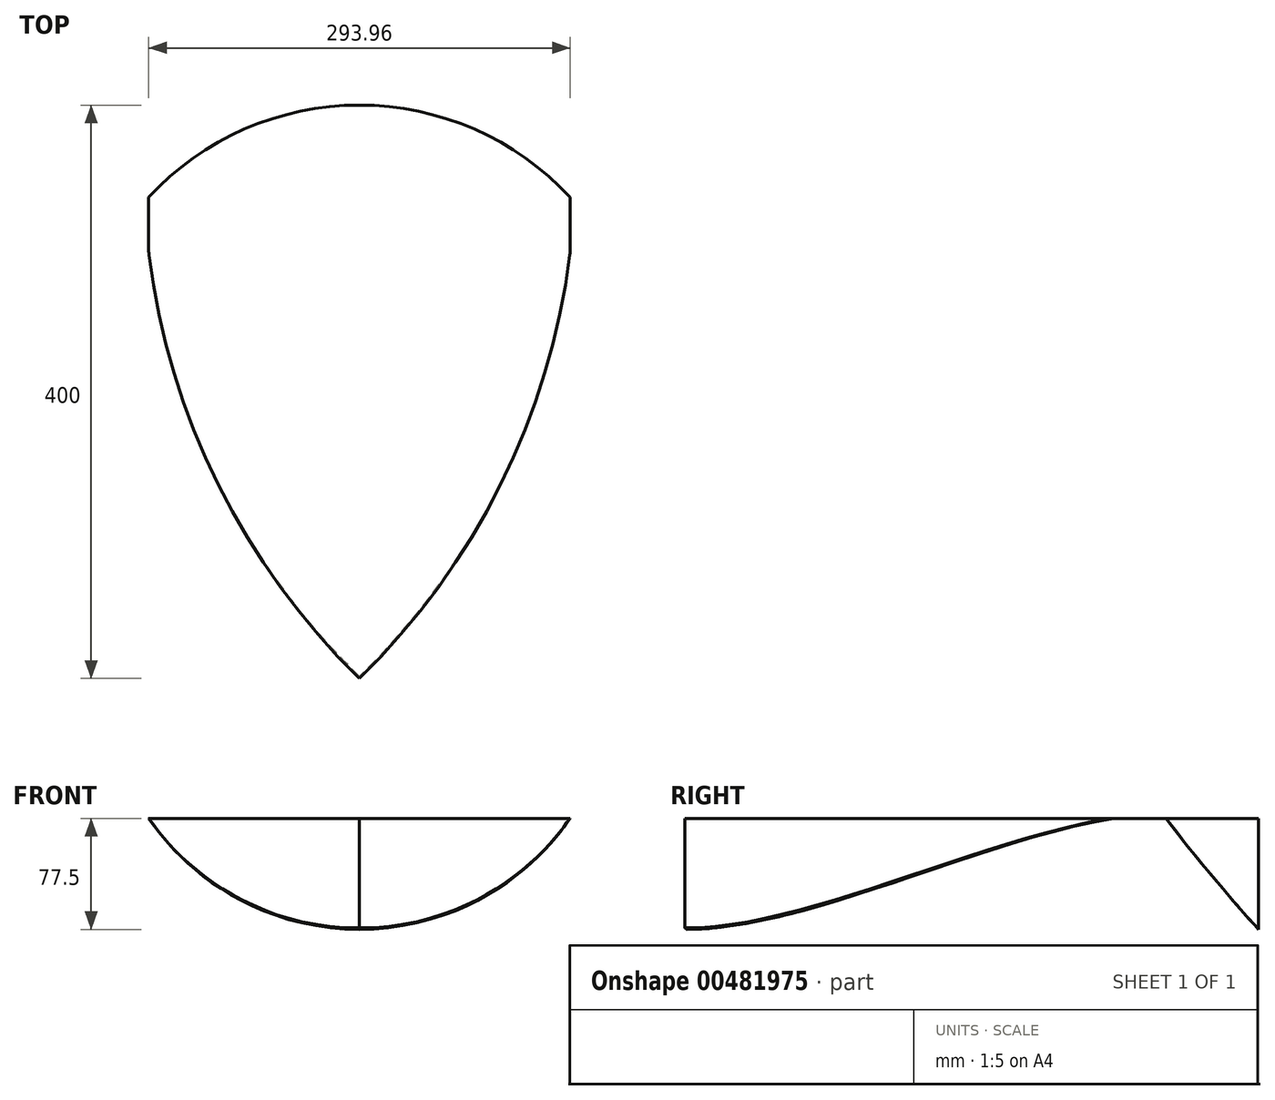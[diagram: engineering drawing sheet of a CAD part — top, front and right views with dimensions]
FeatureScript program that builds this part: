
annotation { "Feature Type Name" : "Feature", "Feature Type Description" : "" }
export const myFeature = defineFeature(function(context is Context, id is Id, definition is map)
    precondition{}
    {
        {
            var Q0;
            Q0=qCreatedBy(makeId("Front.planeOp"),FACE);
            var sketch = newSketch(context, id + "F0", { "sketchPlane" : qUnion([Q0])});
            skLineSegment(sketch, "E0", {"start": v(-150, 80) * mm, "end": v(150, 80) * mm});
            skLineSegment(sketch, "E1", {"start": v(0, 80) * mm, "end": v(0, 0) * mm, "construction": true});
            skArc(sketch, "E2", {"start": v(-150, 80) * mm, "mid": v(0, 0) * mm, "end": v(150, 80) * mm});
            skLineSegment(sketch, "E3", {"start": v(0, 0) * mm, "end": v(-231.09, 0) * mm, "construction": true});
            skLineSegment(sketch, "E4", {"start": v(-154.42, 61.21) * mm, "end": v(-48.4, 0) * mm, "construction": true});
            skSolve(sketch);
        }
        {
            var Q0;
            Q0=makeQuery(id+"F0.imprint","IMPRINT",FACE,{"disambiguationData":[TD([[makeQuery(id+"F0.imprint","IMPRINT",EDGE,{"derivedFrom":sQuery(id+"F0.wireOp",EDGE,"E0")}),-1.0]])]});
            extrude(context, id + "F1", {"entities" : qUnion([Q0]), "depth" : 400 * mm});
        }
        {
            var Q0;
            Q0=makeQuery(id+"F1.opExtrude","SWEPT_FACE",FACE,{"disambiguationData":[OSD([sQuery(id+"F0.wireOp",EDGE,"E0")])]});
            var sketch = newSketch(context, id + "F2", { "sketchPlane" : qUnion([Q0])});
            skArc(sketch, "E5", {"start": v(150, -67.71) * mm, "mid": v(0, 0) * mm, "end": v(-150, -67.71) * mm});
            skLineSegment(sketch, "E6", {"start": v(0, 0) * mm, "end": v(0, -400) * mm, "construction": true});
            skArc(sketch, "E7", {"start": v(-150, -67.71) * mm, "mid": v(-106.37, -248.02) * mm, "end": v(0, -400) * mm});
            skArc(sketch, "E8", {"start": v(0, -400) * mm, "mid": v(106.37, -248.02) * mm, "end": v(150, -67.71) * mm});
            skSolve(sketch);
        }
        {
            var Q0;
            {var subQ0=sQuery(id+"F2.wireOp",EDGE,"E5");var subQ2=sQuery(id+"F0.wireOp",EDGE,"E0");var subQ5=makeQuery(id+"F1.opExtrude","CAP_EDGE",EDGE,{"disambiguationData":[OSD([subQ2])],"isStart":true});var subQ6=makeQuery(id+"F2.imprint","INTERSECT",VERTEX,{"derivedFrom":[subQ5,subQ0]});Q0=makeQuery(id+"F2.imprint","IMPRINT",FACE,{"disambiguationData":[TD([[makeQuery(id+"F2.imprint","IMPRINT",EDGE,{"disambiguationData":[TD([[subQ6,1.0]])],"derivedFrom":subQ5}),-1.0]])]});}
            var Q1;
            {var subQ0=sQuery(id+"F2.wireOp",EDGE,"E5");var subQ2=sQuery(id+"F0.wireOp",EDGE,"E0");var subQ5=makeQuery(id+"F1.opExtrude","CAP_EDGE",EDGE,{"disambiguationData":[OSD([subQ2])],"isStart":true});var subQ6=makeQuery(id+"F2.imprint","INTERSECT",VERTEX,{"derivedFrom":[subQ5,subQ0]});Q1=makeQuery(id+"F2.imprint","IMPRINT",FACE,{"disambiguationData":[TD([[makeQuery(id+"F2.imprint","IMPRINT",EDGE,{"disambiguationData":[TD([[subQ6,-1.0]])],"derivedFrom":subQ5}),-1.0]])]});}
            var Q2;
            {var subQ0=sQuery(id+"F2.wireOp",EDGE,"E7");Q2=makeQuery(id+"F2.imprint","IMPRINT",FACE,{"disambiguationData":[TD([[makeQuery(id+"F2.imprint","IMPRINT",EDGE,{"derivedFrom":subQ0}),-1.0]])]});}
            var Q3;
            {var subQ0=sQuery(id+"F2.wireOp",EDGE,"E8");Q3=makeQuery(id+"F2.imprint","IMPRINT",FACE,{"disambiguationData":[TD([[makeQuery(id+"F2.imprint","IMPRINT",EDGE,{"derivedFrom":subQ0}),-1.0]])]});}
            extrude(context, id + "F3", {"entities" : qUnion([Q0, Q1, Q2, Q3]), "operationType" : NewBodyOperationType.REMOVE, "endBound" : BoundingType.THROUGH_ALL, "oppositeDirection" : true, "depth" : 25 * mm});
        }
        {
            var Q0;
            Q0=qCreatedBy(makeId("Front.planeOp"),FACE);
            var sketch = newSketch(context, id + "F4", { "sketchPlane" : qUnion([Q0])});
            skArc(sketch, "E9.0", {"start": v(150, 80) * mm, "mid": v(0, 0) * mm, "end": v(-150, 80) * mm});
            skLineSegment(sketch, "E10.0", {"start": v(150, 80) * mm, "end": v(-150, 80) * mm});
            skArc(sketch, "E11.0", {"start": v(146.98, 80) * mm, "mid": v(0, 2.5) * mm, "end": v(-146.98, 80) * mm});
            skLineSegment(sketch, "E12", {"start": v(146.98, 80) * mm, "end": v(-146.98, 80) * mm});
            skSolve(sketch);
        }
        {
            var Q0;
            Q0=makeQuery(id+"F4.imprint","IMPRINT",FACE,{"disambiguationData":[TD([[makeQuery(id+"F4.imprint","IMPRINT",EDGE,{"derivedFrom":sQuery(id+"F4.wireOp",EDGE,"E11.0")}),-1.0]])]});
            extrude(context, id + "F5", {"entities" : qUnion([Q0]), "operationType" : NewBodyOperationType.REMOVE, "endBound" : BoundingType.THROUGH_ALL, "depth" : 548 * mm});
        }
        {
            var Q0;
            Q0=makeQuery(id+"F3.boolean.opBoolean","COPY",EDGE,{"derivedFrom":makeQuery(id+"F3.opExtrude","CAP_EDGE",EDGE,{"disambiguationData":[OSD([sQuery(id+"F2.wireOp",EDGE,"E7")])],"isStart":true})});
            var Q1;
            {var subQ0=sQuery(id+"F4.wireOp",EDGE,"E12");var subQ1=sQuery(id+"F4.wireOp",EDGE,"E11.0");var subQ2=sQuery(id+"F4.wireOp",EDGE,"E10.0");var subQ3=sQuery(id+"F2.wireOp",EDGE,"E8");var subQ4=sQuery(id+"F2.wireOp",EDGE,"E5");var subQ5=sQuery(id+"F0.wireOp",EDGE,"E2");var subQ6=sQuery(id+"F0.wireOp",EDGE,"E0");Q1=makeQuery(id+"F5.boolean.opBoolean","MERGE",EDGE,{"derivedFrom":[makeQuery(id+"FgXq82e7jWQJ7g4_1.opShell","SHELL_CAP_EDGE",EDGE,{"derivedFrom":[makeQuery(id+"F3.boolean.opBoolean","TWEAK_VERTEX",VERTEX,{"derivedFrom":[makeQuery(id+"F3.opExtrude","CAP_VERTEX",VERTEX,{"disambiguationData":[OSD([subQ6,subQ5,subQ4,subQ3]),ownerDisambiguation([makeQuery(id+"F2.imprint","IMPRINT",EDGE,{"disambiguationData":[TD([[makeQuery(id+"F2.imprint","INTERSECT",VERTEX,{"derivedFrom":[makeQuery(id+"F1.opExtrude","CAP_EDGE",EDGE,{"disambiguationData":[OSD([subQ6])],"isStart":true}),subQ4]}),1.0]])],"derivedFrom":subQ4})])],"isStart":true}),makeQuery(id+"F3.opExtrude","CAP_VERTEX",VERTEX,{"disambiguationData":[OSD([subQ6,subQ5,subQ4,subQ3]),ownerDisambiguation([makeQuery(id+"F2.imprint","IMPRINT",EDGE,{"derivedFrom":subQ3})])],"isStart":true})]})]}),makeQuery(id+"F5.opExtrude","SWEPT_EDGE",EDGE,{"disambiguationData":[OSD([subQ2,subQ1,subQ0]),TDD([makeQuery(id+"F4.imprint","INTERSECT",VERTEX,{"disambiguationData":[OD(0.0)],"derivedFrom":[subQ2,subQ1,subQ0]})])]})]});}
            var Q2;
            Q2=makeQuery(id+"F5.boolean.opBoolean","INTERSECT",EDGE,{"derivedFrom":[makeQuery(id+"F3.boolean.opBoolean","COPY",FACE,{"derivedFrom":makeQuery(id+"F3.opExtrude","SWEPT_FACE",FACE,{"disambiguationData":[OSD([sQuery(id+"F2.wireOp",EDGE,"E8")])]})}),makeQuery(id+"F5.opExtrude","SWEPT_FACE",FACE,{"disambiguationData":[OSD([sQuery(id+"F4.wireOp",EDGE,"E11.0")])]})]});
            var Q3;
            Q3=makeQuery(id+"F5.boolean.opBoolean","INTERSECT",EDGE,{"derivedFrom":[makeQuery(id+"F3.boolean.opBoolean","COPY",FACE,{"derivedFrom":makeQuery(id+"F3.opExtrude","SWEPT_FACE",FACE,{"disambiguationData":[OSD([sQuery(id+"F2.wireOp",EDGE,"E7")])]})}),makeQuery(id+"F5.opExtrude","SWEPT_FACE",FACE,{"disambiguationData":[OSD([sQuery(id+"F4.wireOp",EDGE,"E11.0")])]})]});
            var Q4;
            {var subQ0=sQuery(id+"F2.wireOp",EDGE,"E5");var subQ1=sQuery(id+"F0.wireOp",EDGE,"E2");var subQ2=sQuery(id+"F0.wireOp",EDGE,"E0");var subQ3=makeQuery(id+"F2.imprint","INTERSECT",VERTEX,{"derivedFrom":[makeQuery(id+"F1.opExtrude","CAP_EDGE",EDGE,{"disambiguationData":[OSD([subQ2])],"isStart":true}),subQ0]});Q4=makeQuery(id+"F3.boolean.opBoolean","INTERSECT",EDGE,{"derivedFrom":[makeQuery(id+"F1.opExtrude","SWEPT_FACE",FACE,{"disambiguationData":[OSD([subQ1])]}),makeQuery(id+"F3.opExtrude","SWEPT_FACE",FACE,{"disambiguationData":[OSD([subQ0]),TDD([makeQuery(id+"F2.imprint","IMPRINT",EDGE,{"disambiguationData":[TD([[subQ3,1.0]])],"derivedFrom":subQ0})])]}),makeQuery(id+"F3.opExtrude","SWEPT_FACE",FACE,{"disambiguationData":[OSD([subQ0]),TDD([makeQuery(id+"F2.imprint","IMPRINT",EDGE,{"disambiguationData":[TD([[subQ3,-1.0]])],"derivedFrom":subQ0})])]})]});}
            var Q5;
            {var subQ0=sQuery(id+"F2.wireOp",EDGE,"E5");var subQ2=sQuery(id+"F0.wireOp",EDGE,"E0");var subQ3=makeQuery(id+"F2.imprint","INTERSECT",VERTEX,{"derivedFrom":[makeQuery(id+"F1.opExtrude","CAP_EDGE",EDGE,{"disambiguationData":[OSD([subQ2])],"isStart":true}),subQ0]});Q5=makeQuery(id+"F5.boolean.opBoolean","INTERSECT",EDGE,{"derivedFrom":[makeQuery(id+"F3.boolean.opBoolean","TWEAK_FACE",FACE,{"derivedFrom":[makeQuery(id+"F3.opExtrude","SWEPT_FACE",FACE,{"disambiguationData":[OSD([subQ0]),TDD([makeQuery(id+"F2.imprint","IMPRINT",EDGE,{"disambiguationData":[TD([[subQ3,1.0]])],"derivedFrom":subQ0})])]}),makeQuery(id+"F3.opExtrude","SWEPT_FACE",FACE,{"disambiguationData":[OSD([subQ0]),TDD([makeQuery(id+"F2.imprint","IMPRINT",EDGE,{"disambiguationData":[TD([[subQ3,-1.0]])],"derivedFrom":subQ0})])]})]}),makeQuery(id+"F5.opExtrude","SWEPT_FACE",FACE,{"disambiguationData":[OSD([sQuery(id+"F4.wireOp",EDGE,"E11.0")])]})]});}
            chamfer(context, id + "F6", {"entities" : qUnion([Q0, Q1, Q2, Q3, Q4, Q5]), "width" : 1 * mm, "tangentPropagation" : true});
        }
    });
